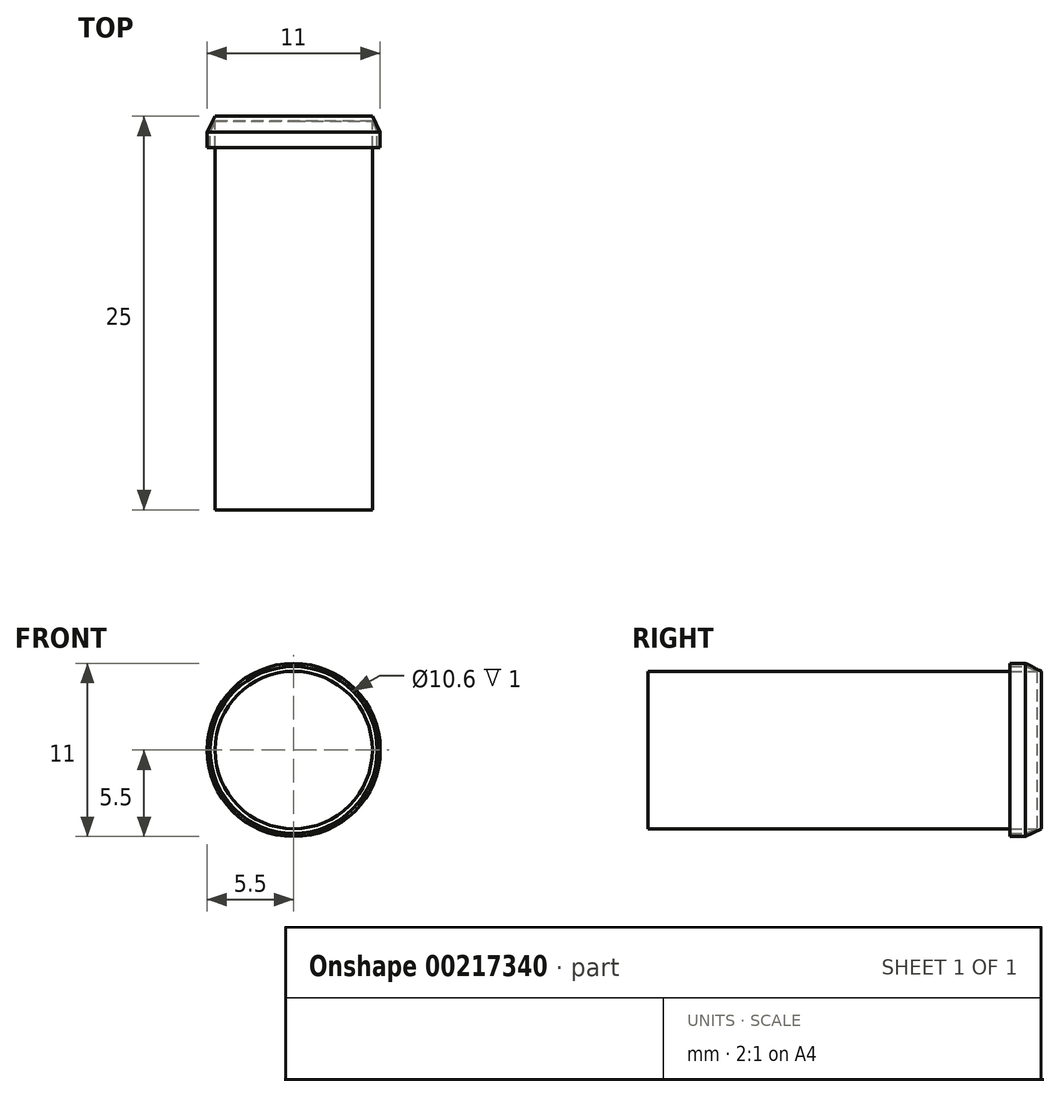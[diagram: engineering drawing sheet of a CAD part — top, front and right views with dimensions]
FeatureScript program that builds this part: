
annotation { "Feature Type Name" : "Feature", "Feature Type Description" : "" }
export const myFeature = defineFeature(function(context is Context, id is Id, definition is map)
    precondition{}
    {
        {
            var Q0;
            Q0=qCreatedBy(makeId("Front.planeOp"),FACE);
            var sketch = newSketch(context, id + "F0", { "sketchPlane" : qUnion([Q0])});
            skCircle(sketch, "E0", {"center": v(0, 0) * mm, "radius": 5 * mm});
            skSolve(sketch);
        }
        {
            var Q0;
            Q0=makeQuery(id+"F0.imprint","IMPRINT",FACE,{"disambiguationData":[TD([[makeQuery(id+"F0.imprint","IMPRINT",EDGE,{"derivedFrom":sQuery(id+"F0.wireOp",EDGE,"E0")}),1.0]])]});
            extrude(context, id + "F1", {"entities" : qUnion([Q0]), "depth" : 25 * mm});
        }
        {
            var Q0;
            Q0=makeQuery(id+"F1.opExtrude","CAP_FACE",FACE,{"disambiguationData":[OSD([sQuery(id+"F0.wireOp",EDGE,"E0")])],"isStart":true});
            var sketch = newSketch(context, id + "F2", { "sketchPlane" : qUnion([Q0])});
            skCircle(sketch, "E1", {"center": v(0, 0) * mm, "radius": 5.5 * mm});
            skSolve(sketch);
        }
        {
            var Q0;
            Q0 = qSketchRegion(id + "F2", true);
            extrude(context, id + "F3", {"entities" : qUnion([Q0]), "operationType" : NewBodyOperationType.ADD, "oppositeDirection" : true, "depth" : 1 * mm});
        }
        {
            var Q0;
            Q0=qCreatedBy(makeId("Right.planeOp"),FACE);
            var sketch = newSketch(context, id + "F4", { "sketchPlane" : qUnion([Q0])});
            skLineSegment(sketch, "E2", {"start": v(-1, 5.5) * mm, "end": v(0, 5) * mm});
            skLineSegment(sketch, "E3", {"start": v(-27.33, 5.5) * mm, "end": v(4.37, 5.5) * mm, "construction": true});
            skLineSegment(sketch, "E4", {"start": v(-29.16, 5) * mm, "end": v(8.45, 5) * mm, "construction": true});
            skLineSegment(sketch, "E5", {"start": v(-1, 5.5) * mm, "end": v(0, 5.5) * mm});
            skLineSegment(sketch, "E6", {"start": v(0, 5.5) * mm, "end": v(0, 5) * mm});
            skLineSegment(sketch, "E7", {"start": v(-35.11, 0) * mm, "end": v(12.82, 0) * mm, "construction": true});
            skSolve(sketch);
        }
        {
            var Q0;
            Q0=makeQuery(id+"F4.imprint","IMPRINT",FACE,{"disambiguationData":[TD([[makeQuery(id+"F4.imprint","IMPRINT",EDGE,{"derivedFrom":sQuery(id+"F4.wireOp",EDGE,"E2")}),1.0]])]});
            var Q1;
            Q1=sQuery(id+"F4.wireOp",EDGE,"E7");
            revolve(context, id + "F5", {"operationType" : NewBodyOperationType.REMOVE, "entities" : qUnion([Q0]), "axis" : qUnion([Q1]), "revolveType" : RevolveType.FULL, "oppositeDirection" : true});
        }
        {
            var Q0;
            Q0=qCreatedBy(makeId("Right.planeOp"),FACE);
            var sketch = newSketch(context, id + "F6", { "sketchPlane" : qUnion([Q0])});
            skLineSegment(sketch, "E8", {"start": v(-31.87, 0) * mm, "end": v(8.8, 0) * mm});
            skLineSegment(sketch, "E9", {"start": v(-35, 5) * mm, "end": v(8.85, 5) * mm, "construction": true});
            skLineSegment(sketch, "E10", {"start": v(-35, 5.3) * mm, "end": v(8.85, 5.3) * mm, "construction": true});
            skLineSegment(sketch, "E11", {"start": v(-1, 6.47) * mm, "end": v(-1, -0.92) * mm, "construction": true});
            skLineSegment(sketch, "E12", {"start": v(-0.3, 6.6) * mm, "end": v(-0.3, -0.64) * mm, "construction": true});
            skLineSegment(sketch, "E13", {"start": v(-0.3, 5) * mm, "end": v(-1, 5.3) * mm});
            skLineSegment(sketch, "E14", {"start": v(-1, 5.3) * mm, "end": v(-1, 5) * mm});
            skLineSegment(sketch, "E15", {"start": v(-1, 5) * mm, "end": v(-0.3, 5) * mm});
            skSolve(sketch);
        }
        {
            var Q0;
            Q0 = qSketchRegion(id + "F6", true);
            var Q1;
            Q1=sQuery(id+"F6.wireOp",EDGE,"E8");
            revolve(context, id + "F7", {"operationType" : NewBodyOperationType.REMOVE, "entities" : qUnion([Q0]), "axis" : qUnion([Q1]), "revolveType" : RevolveType.FULL, "oppositeDirection" : true});
        }
        {
            var Q0;
            Q0=makeQuery(id+"F3.opExtrude","CAP_FACE",FACE,{"disambiguationData":[OSD([sQuery(id+"F2.wireOp",EDGE,"E1")])],"isStart":false});
            var sketch = newSketch(context, id + "F8", { "sketchPlane" : qUnion([Q0])});
            skCircle(sketch, "E16", {"center": v(0, 0) * mm, "radius": 5.5 * mm});
            skCircle(sketch, "E17", {"center": v(0, 0) * mm, "radius": 5.3 * mm});
            skSolve(sketch);
        }
        {
            var Q0;
            Q0=makeQuery(id+"F8.imprint","IMPRINT",FACE,{"disambiguationData":[TD([[makeQuery(id+"F8.imprint","IMPRINT",EDGE,{"derivedFrom":sQuery(id+"F8.wireOp",EDGE,"E16")}),-1.0]])]});
            extrude(context, id + "F9", {"entities" : qUnion([Q0]), "operationType" : NewBodyOperationType.ADD, "depth" : 1 * mm});
        }
    });
